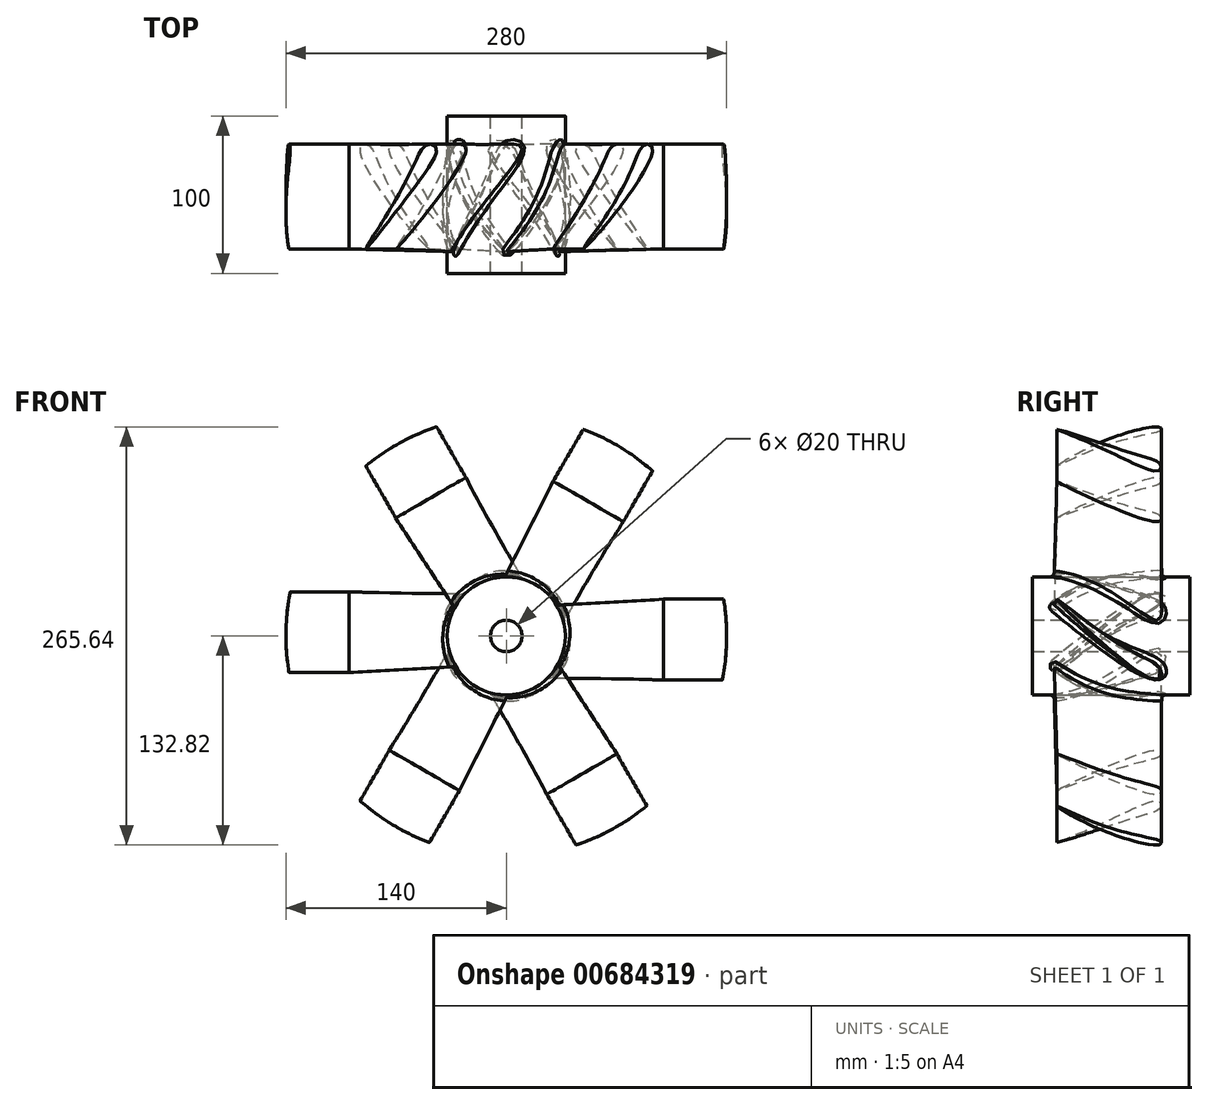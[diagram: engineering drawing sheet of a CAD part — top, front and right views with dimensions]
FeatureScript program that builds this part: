
annotation { "Feature Type Name" : "Feature", "Feature Type Description" : "" }
export const myFeature = defineFeature(function(context is Context, id is Id, definition is map)
    precondition{}
    {
        {
            var Q0;
            Q0=qCreatedBy(makeId("Front.planeOp"),FACE);
            var sketch = newSketch(context, id + "F0", { "sketchPlane" : qUnion([Q0])});
            skCircle(sketch, "E0", {"center": v(0, 0) * mm, "radius": 37.5 * mm});
            skSolve(sketch);
        }
        {
            var Q0;
            Q0=makeQuery(id+"F0.imprint","IMPRINT",FACE,{"disambiguationData":[TD([[makeQuery(id+"F0.imprint","IMPRINT",EDGE,{"derivedFrom":sQuery(id+"F0.wireOp",EDGE,"E0")}),1.0]])]});
            extrude(context, id + "F1", {"entities" : qUnion([Q0]), "endBound" : BoundingType.SYMMETRIC, "depth" : 100 * mm, "offsetDistance" : 25 * mm});
        }
        {
            var Q0;
            Q0=qCreatedBy(makeId("Right.planeOp"),FACE);
            var sketch = newSketch(context, id + "F2", { "sketchPlane" : qUnion([Q0])});
            skFitSpline(sketch, "E1", {"points": [v(-36.93, 17.7) * mm, v(29.67, -27.49) * mm, v(31.3, -21.14) * mm, v(0, -6.44) * mm, v(-36.93, 17.7) * mm]});
            skSolve(sketch);
        }
        {
            var Q0;
            Q0=qCreatedBy(makeId("Right.planeOp"),FACE);
            cPlane(context, id + "F3", {"entities" : qUnion([Q0]), "cplaneType" : CPlaneType.OFFSET, "offset" : 100 * mm, "width" : 150 * mm, "height" : 150 * mm});
        }
        {
            var Q0;
            Q0=qCreatedBy(id+"F3.planeOp",FACE);
            var sketch = newSketch(context, id + "F4", { "sketchPlane" : qUnion([Q0])});
            skFitSpline(sketch, "E2", {"points": [v(-34.39, 22.95) * mm, v(25.68, -27.49) * mm, v(31.84, -25.5) * mm, v(30.4, -19.69) * mm, v(19.69, -13.16) * mm, v(-13.7, 7.71) * mm, v(-34.39, 22.95) * mm]});
            skSolve(sketch);
        }
        {
            var Q1;
            Q1 = qSketchRegion(id + "F2", true);
            var Q2;
            Q2 = qSketchRegion(id + "F4", true);
            loft(context, id + "F5", {"operationType" : NewBodyOperationType.ADD, "sheetProfilesArray" : [{ "sheetProfileEntities" : qUnion([Q1]) }, { "sheetProfileEntities" : qUnion([Q2]) }]});
        }
        {
            var Q0;
            Q0=makeQuery(id+"F5.opLoft","CAP_FACE",FACE,{"disambiguationData":[OSD([makeQuery(id+"F4.imprint","IMPRINT",FACE,{"disambiguationData":[TD([[makeQuery(id+"F4.imprint","IMPRINT",EDGE,{"derivedFrom":sQuery(id+"F4.wireOp",EDGE,"E2")}),1.0]])]})])],"isStart":true});
            extrude(context, id + "F6", {"entities" : qUnion([Q0]), "operationType" : NewBodyOperationType.ADD, "depth" : 50 * mm, "offsetDistance" : 25 * mm});
        }
        {
            var Q0;
            Q0=makeQuery(id+"F1.opExtrude","SWEPT_BODY",BODY,{"disambiguationData":[OSD([sQuery(id+"F0.wireOp",EDGE,"E0")])]});
            var Q1;
            Q1=makeQuery(id+"F1.opExtrude","CAP_EDGE",EDGE,{"disambiguationData":[OSD([sQuery(id+"F0.wireOp",EDGE,"E0")])],"isStart":true});
            circularPattern(context, id + "F7", {"entities" : qUnion([Q0]), "axis" : qUnion([Q1]), "angle" : 360 * degree, "instanceCount" : 6, "equalSpace" : true});
        }
        {
            var Q0;
            Q0=qCreatedBy(makeId("Front.planeOp"),FACE);
            cPlane(context, id + "F8", {"entities" : qUnion([Q0]), "cplaneType" : CPlaneType.OFFSET, "offset" : 50 * mm, "oppositeDirection" : true, "width" : 150 * mm, "height" : 150 * mm});
        }
        {
            var Q0;
            Q0=qCreatedBy(id+"F8.planeOp",FACE);
            var sketch = newSketch(context, id + "F9", { "sketchPlane" : qUnion([Q0])});
            skCircle(sketch, "E3", {"center": v(0, 0) * mm, "radius": 10 * mm});
            skSolve(sketch);
        }
        {
            var Q0;
            Q0=makeQuery(id+"F9.imprint","IMPRINT",FACE,{"disambiguationData":[TD([[makeQuery(id+"F9.imprint","IMPRINT",EDGE,{"derivedFrom":sQuery(id+"F9.wireOp",EDGE,"E3")}),1.0]])]});
            extrude(context, id + "F10", {"entities" : qUnion([Q0]), "operationType" : NewBodyOperationType.REMOVE, "depth" : 210 * mm, "offsetDistance" : 25 * mm});
        }
        {
            var Q0;
            Q0=makeQuery(id+"F7.opPattern","COPY",EDGE,{"derivedFrom":makeQuery(id+"F5.boolean.opBoolean","INTERSECT",EDGE,{"derivedFrom":[makeQuery(id+"F1.opExtrude","SWEPT_FACE",FACE,{"disambiguationData":[OSD([sQuery(id+"F0.wireOp",EDGE,"E0")])]}),makeQuery(id+"F5.opLoft","SWEPT_FACE",FACE,{"disambiguationData":[OSD([sQuery(id+"F2.wireOp",EDGE,"E1"),sQuery(id+"F4.wireOp",EDGE,"E2")])]})]}),"instanceName":"2"});
            fillet(context, id + "F11", {"entities" : qUnion([Q0]), "radius" : 3 * mm, "tangentPropagation" : true, "allowEdgeOverflow" : false});
        }
        {
            var Q0;
            Q0=makeQuery(id+"F7.opPattern","COPY",EDGE,{"derivedFrom":makeQuery(id+"F5.boolean.opBoolean","INTERSECT",EDGE,{"derivedFrom":[makeQuery(id+"F1.opExtrude","SWEPT_FACE",FACE,{"disambiguationData":[OSD([sQuery(id+"F0.wireOp",EDGE,"E0")])]}),makeQuery(id+"F5.opLoft","SWEPT_FACE",FACE,{"disambiguationData":[OSD([sQuery(id+"F2.wireOp",EDGE,"E1"),sQuery(id+"F4.wireOp",EDGE,"E2")])]})]}),"instanceName":"1"});
            fillet(context, id + "F12", {"entities" : qUnion([Q0]), "radius" : 3 * mm, "tangentPropagation" : true, "allowEdgeOverflow" : false});
        }
        {
            var Q0;
            Q0=makeQuery(id+"F7.opPattern","COPY",EDGE,{"derivedFrom":makeQuery(id+"F5.boolean.opBoolean","INTERSECT",EDGE,{"derivedFrom":[makeQuery(id+"F1.opExtrude","SWEPT_FACE",FACE,{"disambiguationData":[OSD([sQuery(id+"F0.wireOp",EDGE,"E0")])]}),makeQuery(id+"F5.opLoft","SWEPT_FACE",FACE,{"disambiguationData":[OSD([sQuery(id+"F2.wireOp",EDGE,"E1"),sQuery(id+"F4.wireOp",EDGE,"E2")])]})]}),"instanceName":"3"});
            fillet(context, id + "F13", {"entities" : qUnion([Q0]), "radius" : 3 * mm, "tangentPropagation" : true, "allowEdgeOverflow" : false});
        }
        {
            var Q0;
            Q0=makeQuery(id+"F7.opPattern","COPY",EDGE,{"derivedFrom":makeQuery(id+"F5.boolean.opBoolean","INTERSECT",EDGE,{"derivedFrom":[makeQuery(id+"F1.opExtrude","SWEPT_FACE",FACE,{"disambiguationData":[OSD([sQuery(id+"F0.wireOp",EDGE,"E0")])]}),makeQuery(id+"F5.opLoft","SWEPT_FACE",FACE,{"disambiguationData":[OSD([sQuery(id+"F2.wireOp",EDGE,"E1"),sQuery(id+"F4.wireOp",EDGE,"E2")])]})]}),"instanceName":"4"});
            fillet(context, id + "F14", {"entities" : qUnion([Q0]), "radius" : 3 * mm, "tangentPropagation" : true, "allowEdgeOverflow" : false});
        }
        {
            var Q0;
            Q0=makeQuery(id+"F7.opPattern","COPY",EDGE,{"derivedFrom":makeQuery(id+"F5.boolean.opBoolean","INTERSECT",EDGE,{"derivedFrom":[makeQuery(id+"F1.opExtrude","SWEPT_FACE",FACE,{"disambiguationData":[OSD([sQuery(id+"F0.wireOp",EDGE,"E0")])]}),makeQuery(id+"F5.opLoft","SWEPT_FACE",FACE,{"disambiguationData":[OSD([sQuery(id+"F2.wireOp",EDGE,"E1"),sQuery(id+"F4.wireOp",EDGE,"E2")])]})]}),"instanceName":"5"});
            fillet(context, id + "F15", {"entities" : qUnion([Q0]), "radius" : 3 * mm, "tangentPropagation" : true, "allowEdgeOverflow" : false});
        }
        {
            var Q0;
            Q0=makeQuery(id+"F5.boolean.opBoolean","INTERSECT",EDGE,{"derivedFrom":[makeQuery(id+"F1.opExtrude","SWEPT_FACE",FACE,{"disambiguationData":[OSD([sQuery(id+"F0.wireOp",EDGE,"E0")])]}),makeQuery(id+"F5.opLoft","SWEPT_FACE",FACE,{"disambiguationData":[OSD([sQuery(id+"F2.wireOp",EDGE,"E1"),sQuery(id+"F4.wireOp",EDGE,"E2")])]})]});
            fillet(context, id + "F16", {"entities" : qUnion([Q0]), "radius" : 3 * mm, "tangentPropagation" : true, "allowEdgeOverflow" : false});
        }
        {
            var Q0;
            Q0=makeQuery(id+"F1.opExtrude","CAP_FACE",FACE,{"disambiguationData":[OSD([sQuery(id+"F0.wireOp",EDGE,"E0")])],"isStart":true});
            var sketch = newSketch(context, id + "F17", { "sketchPlane" : qUnion([Q0])});
            skCircle(sketch, "E4", {"center": v(0, 0) * mm, "radius": 140 * mm});
            skSolve(sketch);
        }
        {
            var Q0;
            Q0 = qSketchRegion(id + "F17", true);
            extrude(context, id + "F18", {"entities" : qUnion([Q0]), "operationType" : NewBodyOperationType.INTERSECT, "oppositeDirection" : true, "depth" : 155 * mm, "offsetDistance" : 25 * mm});
        }
    });
